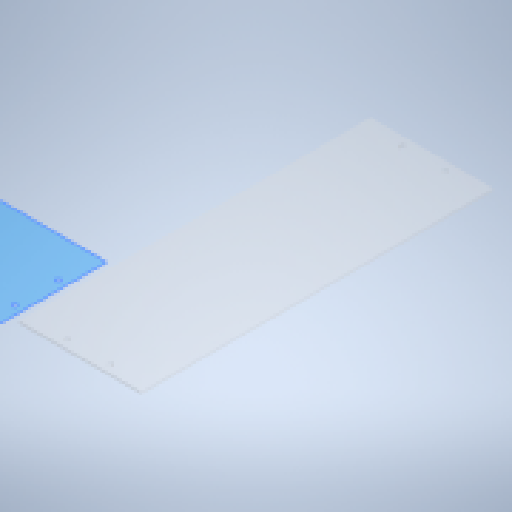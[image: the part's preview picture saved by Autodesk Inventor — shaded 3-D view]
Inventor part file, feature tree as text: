
AUTODESK INVENTOR PART (.ipt)
format: ipt  version: 2024 (Build 280153000, 153)  size: 154,624 bytes
history: native  units: mm
features: extrude x2, sketch x2, other x1
ambient origin geometry x8: Origin, YZ Plane, XZ Plane, XY Plane, X Axis, Y Axis, Z Axis, Center Point
bodies: Body1 (feature_tree)
feature tree (5):
  other  "솔리드1"
  extrude  "돌출1"  Depth=136.0mm
  extrude  "돌출2"  Depth=390.0mm
  sketch  "스케치1"
  sketch  "스케치2"
